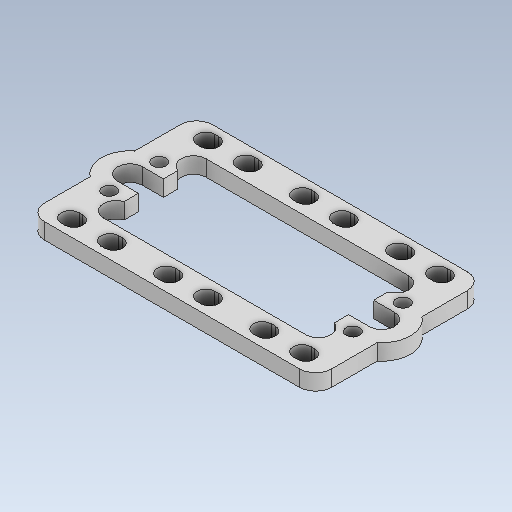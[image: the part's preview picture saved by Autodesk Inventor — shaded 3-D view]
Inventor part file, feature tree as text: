
AUTODESK INVENTOR PART (.ipt)
format: ipt  version: 2020.1 (Build 241239000, 239)  size: 181,248 bytes
history: native  units: in
note: dims shown in document units (in); Inventor stores cm internally (conversion verified against a paired STEP export)
features: mirror x1
ambient origin geometry x8: Origin, YZ Plane, XZ Plane, XY Plane, X Axis, Y Axis, Z Axis, Center Point
bodies: Solid1 (feature_tree)
feature tree (1):
  mirror  "Mirror2"
